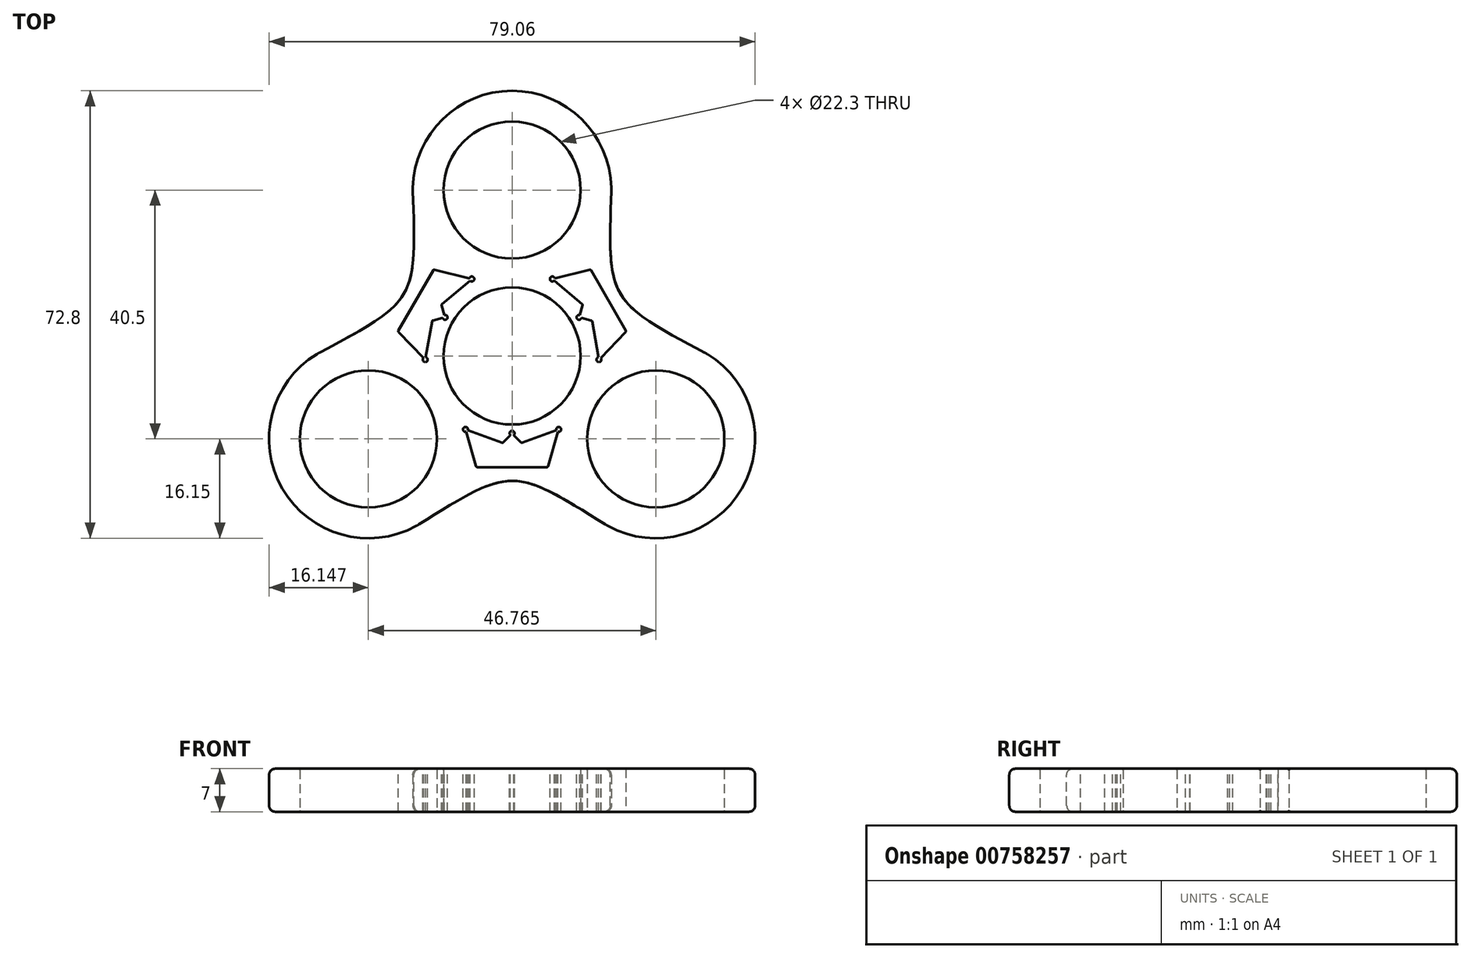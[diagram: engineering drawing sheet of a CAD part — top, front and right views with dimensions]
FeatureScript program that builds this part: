
annotation { "Feature Type Name" : "Feature", "Feature Type Description" : "" }
export const myFeature = defineFeature(function(context is Context, id is Id, definition is map)
    precondition{}
    {
        {
            var Q0;
            Q0=qCreatedBy(makeId("Top.planeOp"),FACE);
            var sketch = newSketch(context, id + "F0", { "sketchPlane" : qUnion([Q0])});
            skCircle(sketch, "E0", {"center": v(0, 0) * mm, "radius": 11.15 * mm});
            skLineSegment(sketch, "E1.0", {"start": v(-15.15, 0) * mm, "end": v(-15.15, 0) * mm});
            skLineSegment(sketch, "E2", {"start": v(0, 0) * mm, "end": v(0, 27) * mm, "construction": true});
            skCircle(sketch, "E3", {"center": v(0, 27) * mm, "radius": 11.15 * mm});
            skArc(sketch, "E4.0", {"start": v(16.15, 27) * mm, "mid": v(0, 43.15) * mm, "end": v(-16.15, 27) * mm});
            skLineSegment(sketch, "E5", {"start": v(-15.15, 0) * mm, "end": v(15.15, 0) * mm, "construction": true});
            skLineSegment(sketch, "E6", {"start": v(-16.15, 27) * mm, "end": v(16.15, 27) * mm, "construction": true});
            skPoint(sketch, "E7.trimOffspring.end.orphan", {"position": v(-15.15, 0) * mm});
            skLineSegment(sketch, "E8", {"start": v(-16.15, 27) * mm, "end": v(-16.15, 27) * mm});
            skArc(sketch, "E9.trimOffspring", {"start": v(-15.15, 0) * mm, "mid": v(0, -15.15) * mm, "end": v(15.15, 0) * mm, "construction": true});
            skLineSegment(sketch, "E10.trimOffspring", {"start": v(16.15, 27) * mm, "end": v(16.15, 27) * mm});
            skLineSegment(sketch, "E11.anchor1", {"start": v(0, 27) * mm, "end": v(0, 43.15) * mm, "construction": true});
            skLineSegment(sketch, "E11.anchor2", {"start": v(0, 27) * mm, "end": v(13.23, 36.26) * mm, "construction": true});
            skLineSegment(sketch, "E12.1.0", {"start": v(7.57, -13.12) * mm, "end": v(-7.58, 13.12) * mm, "construction": true});
            skLineSegment(sketch, "E12.1.2", {"start": v(0, 0) * mm, "end": v(-23.38, -13.5) * mm, "construction": true});
            skLineSegment(sketch, "E12.1.4", {"start": v(-15.3, -27.49) * mm, "end": v(-31.46, 0.49) * mm, "construction": true});
            skCircle(sketch, "E12.1.5", {"center": v(-23.38, -13.5) * mm, "radius": 11.15 * mm});
            skPoint(sketch, "E12.1.9", {"position": v(7.57, -13.12) * mm});
            skArc(sketch, "E12.1.14", {"start": v(-31.46, 0.49) * mm, "mid": v(-37.37, -21.57) * mm, "end": v(-15.3, -27.49) * mm});
            skLineSegment(sketch, "E12.2.0", {"start": v(7.57, 13.12) * mm, "end": v(-7.58, -13.12) * mm, "construction": true});
            skLineSegment(sketch, "E12.2.2", {"start": v(0, 0) * mm, "end": v(23.38, -13.5) * mm, "construction": true});
            skLineSegment(sketch, "E12.2.4", {"start": v(31.46, 0.49) * mm, "end": v(15.3, -27.49) * mm, "construction": true});
            skCircle(sketch, "E12.2.5", {"center": v(23.38, -13.5) * mm, "radius": 11.15 * mm});
            skArc(sketch, "E12.2.12", {"start": v(7.57, 13.12) * mm, "mid": v(-13.12, 7.57) * mm, "end": v(-7.58, -13.12) * mm, "construction": true});
            skArc(sketch, "E12.2.14", {"start": v(15.3, -27.49) * mm, "mid": v(37.37, -21.57) * mm, "end": v(31.46, 0.49) * mm});
            skFitSpline(sketch, "E13", {"points": [v(16.15, 27) * mm, v(31.46, 0.49) * mm], "startDerivative": vector(-1.87, -54.1) * mm, "endDerivative": vector(47.8, -25.43) * mm});
            skLineSegment(sketch, "E14", {"start": v(0, 0) * mm, "end": v(26.97, 15.57) * mm, "construction": true});
            skLineSegment(sketch, "E15", {"start": v(-15.3, -27.49) * mm, "end": v(-3.01, -11.46) * mm});
            skLineSegment(sketch, "E16", {"start": v(-3.01, -11.46) * mm, "end": v(3.36, -11.46) * mm});
            skLineSegment(sketch, "E17", {"start": v(3.36, -11.46) * mm, "end": v(15.3, -27.49) * mm});
            skLineSegment(sketch, "E18", {"start": v(-31.46, 0.49) * mm, "end": v(-13.47, 2.14) * mm});
            skLineSegment(sketch, "E19", {"start": v(-13.47, 2.14) * mm, "end": v(-9.18, 9.2) * mm});
            skLineSegment(sketch, "E20", {"start": v(-9.18, 9.2) * mm, "end": v(-16.15, 27) * mm});
            skSolve(sketch);
        }
        {
            var Q0;
            Q0=qCreatedBy(makeId("Right.planeOp"),FACE);
            var sketch = newSketch(context, id + "F1", { "sketchPlane" : qUnion([Q0])});
            skLineSegment(sketch, "E21", {"start": v(0, 18.91) * mm, "end": v(0, -18.72) * mm, "construction": true});
            skSolve(sketch);
        }
        {
            var Q0;
            Q0=makeQuery(id+"F0.imprint","IMPRINT",FACE,{"disambiguationData":[TD([[makeQuery(id+"F0.imprint","IMPRINT",EDGE,{"derivedFrom":sQuery(id+"F0.wireOp",EDGE,"E0")}),-1.0]])]});
            var Q1;
            Q1=makeQuery(id+"F0.imprint","IMPRINT",FACE,{"disambiguationData":[TD([[makeQuery(id+"F0.imprint","IMPRINT",EDGE,{"derivedFrom":sQuery(id+"F0.wireOp",EDGE,"E3")}),-1.0]])]});
            extrude(context, id + "F2", {"entities" : qUnion([Q0, Q1]), "depth" : 7 * mm, "offsetDistance" : 25 * mm});
        }
        {
            var Q0;
            Q0=makeQuery(id+"F2.opExtrude","SWEPT_BODY",BODY,{"disambiguationData":[OSD([sQuery(id+"F0.wireOp",EDGE,"E0"),sQuery(id+"F0.wireOp",EDGE,"E1.0"),sQuery(id+"F0.wireOp",EDGE,"E3"),sQuery(id+"F0.wireOp",EDGE,"E4.0"),sQuery(id+"F0.wireOp",EDGE,"oIW5whhO-fQ4n-saJ2-gWf4-q0JPziCMkqRt"),sQuery(id+"F0.wireOp",EDGE,"e7664bf7-e720-472f-93c8-efa73fce652a0.MirrorCS"),sQuery(id+"F0.wireOp",EDGE,"15db0cb3-5bd8-46cc-a881-ea2e00802e11.filletArc"),sQuery(id+"F0.wireOp",EDGE,"163ba6b5-26b9-4c58-8659-ca6763b85cf9.filletArc")])]});
            var Q1;
            Q1=sQuery(id+"F1.wireOp",EDGE,"E21");
            circularPattern(context, id + "F3", {"operationType" : NewBodyOperationType.ADD, "entities" : qUnion([Q0]), "axis" : qUnion([Q1]), "angle" : 360 * degree, "instanceCount" : 3, "equalSpace" : true});
        }
        {
            var Q0;
            Q0=makeQuery(id+"F2.opExtrude","SWEPT_EDGE",EDGE,{"disambiguationData":[OSD([sQuery(id+"F0.wireOp",EDGE,"E4.0"),sQuery(id+"F0.wireOp",EDGE,"E13")])]});
            var Q1;
            Q1=makeQuery(id+"F2.opExtrude","SWEPT_EDGE",EDGE,{"disambiguationData":[OSD([sQuery(id+"F0.wireOp",EDGE,"E12.2.14"),sQuery(id+"F0.wireOp",EDGE,"E13")])]});
            var Q2;
            Q2=makeQuery(id+"F3.boolean.opBoolean","MERGE",EDGE,{"derivedFrom":[makeQuery(id+"F2.opExtrude","SWEPT_EDGE",EDGE,{"disambiguationData":[OSD([sQuery(id+"F0.wireOp",EDGE,"E12.2.14"),sQuery(id+"F0.wireOp",EDGE,"E17")])]}),makeQuery(id+"F3.opPattern","COPY",EDGE,{"derivedFrom":makeQuery(id+"F2.opExtrude","SWEPT_EDGE",EDGE,{"disambiguationData":[OSD([sQuery(id+"F0.wireOp",EDGE,"E4.0"),sQuery(id+"F0.wireOp",EDGE,"E13")])]}),"instanceName":"1"})]});
            var Q3;
            Q3=makeQuery(id+"F3.boolean.opBoolean","MERGE",EDGE,{"derivedFrom":[makeQuery(id+"F2.opExtrude","SWEPT_EDGE",EDGE,{"disambiguationData":[OSD([sQuery(id+"F0.wireOp",EDGE,"E12.1.14"),sQuery(id+"F0.wireOp",EDGE,"E15")])]}),makeQuery(id+"F3.opPattern","COPY",EDGE,{"derivedFrom":makeQuery(id+"F2.opExtrude","SWEPT_EDGE",EDGE,{"disambiguationData":[OSD([sQuery(id+"F0.wireOp",EDGE,"E12.2.14"),sQuery(id+"F0.wireOp",EDGE,"E13")])]}),"instanceName":"1"})]});
            var Q4;
            Q4=makeQuery(id+"F3.boolean.opBoolean","MERGE",EDGE,{"derivedFrom":[makeQuery(id+"F2.opExtrude","SWEPT_EDGE",EDGE,{"disambiguationData":[OSD([sQuery(id+"F0.wireOp",EDGE,"E12.1.14"),sQuery(id+"F0.wireOp",EDGE,"E18")])]}),makeQuery(id+"F3.opPattern","COPY",EDGE,{"derivedFrom":makeQuery(id+"F2.opExtrude","SWEPT_EDGE",EDGE,{"disambiguationData":[OSD([sQuery(id+"F0.wireOp",EDGE,"E12.2.14"),sQuery(id+"F0.wireOp",EDGE,"E17")])]}),"instanceName":"1"}),makeQuery(id+"F3.opPattern","COPY",EDGE,{"derivedFrom":makeQuery(id+"F2.opExtrude","SWEPT_EDGE",EDGE,{"disambiguationData":[OSD([sQuery(id+"F0.wireOp",EDGE,"E4.0"),sQuery(id+"F0.wireOp",EDGE,"E13")])]}),"instanceName":"2"})]});
            var Q5;
            Q5=makeQuery(id+"F3.boolean.opBoolean","MERGE",EDGE,{"derivedFrom":[makeQuery(id+"F2.opExtrude","SWEPT_EDGE",EDGE,{"disambiguationData":[OSD([sQuery(id+"F0.wireOp",EDGE,"E4.0"),sQuery(id+"F0.wireOp",EDGE,"E20")])]}),makeQuery(id+"F3.opPattern","COPY",EDGE,{"derivedFrom":makeQuery(id+"F2.opExtrude","SWEPT_EDGE",EDGE,{"disambiguationData":[OSD([sQuery(id+"F0.wireOp",EDGE,"E12.1.14"),sQuery(id+"F0.wireOp",EDGE,"E15")])]}),"instanceName":"1"}),makeQuery(id+"F3.opPattern","COPY",EDGE,{"derivedFrom":makeQuery(id+"F2.opExtrude","SWEPT_EDGE",EDGE,{"disambiguationData":[OSD([sQuery(id+"F0.wireOp",EDGE,"E12.2.14"),sQuery(id+"F0.wireOp",EDGE,"E13")])]}),"instanceName":"2"})]});
            fillet(context, id + "F4", {"entities" : qUnion([Q0, Q1, Q2, Q3, Q4, Q5]), "radius" : 10 * mm, "tangentPropagation" : true, "allowEdgeOverflow" : false});
        }
        {
            var Q0;
            Q0=makeQuery(id+"F2.opExtrude","CAP_EDGE",EDGE,{"disambiguationData":[OSD([sQuery(id+"F0.wireOp",EDGE,"E13")])],"isStart":false});
            var Q1;
            Q1=makeQuery(id+"F3.opPattern","COPY",EDGE,{"derivedFrom":makeQuery(id+"F2.opExtrude","CAP_EDGE",EDGE,{"disambiguationData":[OSD([sQuery(id+"F0.wireOp",EDGE,"E13")])],"isStart":false}),"instanceName":"2"});
            var Q2;
            Q2=makeQuery(id+"F3.opPattern","COPY",EDGE,{"derivedFrom":makeQuery(id+"F2.opExtrude","CAP_EDGE",EDGE,{"disambiguationData":[OSD([sQuery(id+"F0.wireOp",EDGE,"E13")])],"isStart":false}),"instanceName":"1"});
            var Q3;
            Q3=makeQuery(id+"F3.opPattern","COPY",EDGE,{"derivedFrom":makeQuery(id+"F2.opExtrude","CAP_EDGE",EDGE,{"disambiguationData":[OSD([sQuery(id+"F0.wireOp",EDGE,"E13")])],"isStart":true}),"instanceName":"2"});
            var Q4;
            Q4=makeQuery(id+"F2.opExtrude","CAP_EDGE",EDGE,{"disambiguationData":[OSD([sQuery(id+"F0.wireOp",EDGE,"E13")])],"isStart":true});
            fillet(context, id + "F5", {"entities" : qUnion([Q0, Q1, Q2, Q3, Q4]), "radius" : 1 * mm, "tangentPropagation" : true, "allowEdgeOverflow" : false});
        }
        {
            var Q0;
            {var subQ0=makeQuery(id+"F2.opExtrude","CAP_FACE",FACE,{"disambiguationData":[OSD([sQuery(id+"F0.wireOp",EDGE,"E0"),sQuery(id+"F0.wireOp",EDGE,"E3"),sQuery(id+"F0.wireOp",EDGE,"E4.0"),sQuery(id+"F0.wireOp",EDGE,"E12.1.5"),sQuery(id+"F0.wireOp",EDGE,"E12.1.14"),sQuery(id+"F0.wireOp",EDGE,"E12.2.5"),sQuery(id+"F0.wireOp",EDGE,"E12.2.14"),sQuery(id+"F0.wireOp",EDGE,"E13"),sQuery(id+"F0.wireOp",EDGE,"E15"),sQuery(id+"F0.wireOp",EDGE,"E16"),sQuery(id+"F0.wireOp",EDGE,"E17"),sQuery(id+"F0.wireOp",EDGE,"E18"),sQuery(id+"F0.wireOp",EDGE,"E19"),sQuery(id+"F0.wireOp",EDGE,"E20")])],"isStart":false});Q0=makeQuery(id+"F3.boolean.opBoolean","MERGE",FACE,{"derivedFrom":[subQ0,makeQuery(id+"F3.opPattern","COPY",FACE,{"derivedFrom":subQ0,"instanceName":"1"}),makeQuery(id+"F3.opPattern","COPY",FACE,{"derivedFrom":subQ0,"instanceName":"2"})]});}
            var sketch = newSketch(context, id + "F6", { "sketchPlane" : qUnion([Q0])});
            skFitSpline(sketch, "E22.0", {"points": [v(30.8, -0.3) * mm, v(29.52, 0.38) * mm, v(27.61, 1.4) * mm, v(25.08, 2.8) * mm, v(23.2, 3.87) * mm, v(21.38, 5.03) * mm, v(19.92, 6.09) * mm, v(18.81, 7.05) * mm, v(17.78, 8.1) * mm, v(17.02, 9.12) * mm, v(16.5, 10.08) * mm, v(16.17, 10.75) * mm, v(15.84, 11.6) * mm, v(15.54, 12.64) * mm, v(15.25, 14.06) * mm, v(15.05, 15.89) * mm, v(14.96, 18.07) * mm, v(14.96, 20.26) * mm, v(15.02, 23.18) * mm, v(15.1, 25.36) * mm, v(15.14, 26.82) * mm], "construction": true});
            skCircle(sketch, "E23.0", {"center": v(0, 0) * mm, "radius": 11.15 * mm, "construction": true});
            skFitSpline(sketch, "E24.0", {"points": [v(29.62, -2.5) * mm, v(28.99, -2.16) * mm, v(27.7, -1.48) * mm, v(25.79, -0.45) * mm, v(23.86, 0.61) * mm, v(21.92, 1.73) * mm, v(20.31, 2.74) * mm, v(19.02, 3.65) * mm, v(18.06, 4.4) * mm, v(17.1, 5.22) * mm, v(16.18, 6.16) * mm, v(15.33, 7.2) * mm, v(14.59, 8.32) * mm, v(13.95, 9.55) * mm, v(13.47, 10.8) * mm, v(13.11, 12.05) * mm, v(12.77, 13.7) * mm, v(12.55, 15.71) * mm, v(12.46, 18.03) * mm, v(12.46, 20.3) * mm, v(12.52, 23.25) * mm, v(12.6, 25.45) * mm, v(12.64, 26.9) * mm], "construction": true});
            skCircle(sketch, "E25.0", {"center": v(0, 27) * mm, "radius": 11.15 * mm, "construction": true});
            skCircle(sketch, "E26.0", {"center": v(23.38, -13.5) * mm, "radius": 11.15 * mm, "construction": true});
            skArc(sketch, "E27.0", {"start": v(13.54, 1.75) * mm, "mid": v(11.82, 6.83) * mm, "end": v(8.28, 10.85) * mm, "construction": true});
            skArc(sketch, "E28.0", {"start": v(18.57, 4) * mm, "mid": v(15.97, 3.07) * mm, "end": v(13.54, 1.75) * mm, "construction": true});
            skArc(sketch, "E29.0", {"start": v(8.28, 10.85) * mm, "mid": v(10.64, 12.3) * mm, "end": v(12.75, 14.08) * mm, "construction": true});
            skLineSegment(sketch, "E30", {"start": v(12.75, 14.08) * mm, "end": v(18.57, 4) * mm});
            skLineSegment(sketch, "E31", {"start": v(15.66, 9.04) * mm, "end": v(10.9, 6.3) * mm, "construction": true});
            skLineSegment(sketch, "E32", {"start": v(18.57, 4) * mm, "end": v(14.4, -0.3) * mm});
            skLineSegment(sketch, "E33", {"start": v(14.06, -0.2) * mm, "end": v(13, 5.77) * mm});
            skLineSegment(sketch, "E34", {"start": v(13, 5.77) * mm, "end": v(11.28, 6.2) * mm});
            skLineSegment(sketch, "E35.MirrorCS", {"start": v(12.75, 14.08) * mm, "end": v(6.94, 12.63) * mm});
            skLineSegment(sketch, "E36.MirrorCS", {"start": v(11.5, 8.37) * mm, "end": v(11, 6.67) * mm});
            skLineSegment(sketch, "E37.MirrorCS", {"start": v(6.86, 12.28) * mm, "end": v(11.5, 8.37) * mm});
            skLineSegment(sketch, "E38", {"start": v(11.5, 8.37) * mm, "end": v(13, 5.77) * mm, "construction": true});
            skArc(sketch, "E39", {"start": v(14.06, -0.2) * mm, "mid": v(14.02, -0.98) * mm, "end": v(14.4, -0.3) * mm});
            skArc(sketch, "E40", {"start": v(11, 6.67) * mm, "mid": v(10.55, 6.1) * mm, "end": v(11.28, 6.2) * mm});
            skArc(sketch, "E41", {"start": v(6.94, 12.63) * mm, "mid": v(6.16, 12.63) * mm, "end": v(6.86, 12.28) * mm});
            skSolve(sketch);
        }
        {
            var Q0;
            Q0=makeQuery(id+"F6.imprint","IMPRINT",FACE,{"disambiguationData":[TD([[makeQuery(id+"F6.imprint","IMPRINT",EDGE,{"derivedFrom":sQuery(id+"F6.wireOp",EDGE,"E30")}),-1.0]])]});
            var Q1;
            {var subQ0=makeQuery(id+"F2.opExtrude","CAP_FACE",FACE,{"disambiguationData":[OSD([sQuery(id+"F0.wireOp",EDGE,"E0"),sQuery(id+"F0.wireOp",EDGE,"E3"),sQuery(id+"F0.wireOp",EDGE,"E4.0"),sQuery(id+"F0.wireOp",EDGE,"E12.1.5"),sQuery(id+"F0.wireOp",EDGE,"E12.1.14"),sQuery(id+"F0.wireOp",EDGE,"E12.2.5"),sQuery(id+"F0.wireOp",EDGE,"E12.2.14"),sQuery(id+"F0.wireOp",EDGE,"E13"),sQuery(id+"F0.wireOp",EDGE,"E15"),sQuery(id+"F0.wireOp",EDGE,"E16"),sQuery(id+"F0.wireOp",EDGE,"E17"),sQuery(id+"F0.wireOp",EDGE,"E18"),sQuery(id+"F0.wireOp",EDGE,"E19"),sQuery(id+"F0.wireOp",EDGE,"E20")])],"isStart":true});Q1=makeQuery(id+"F3.boolean.opBoolean","MERGE",FACE,{"derivedFrom":[subQ0,makeQuery(id+"F3.opPattern","COPY",FACE,{"derivedFrom":subQ0,"instanceName":"1"}),makeQuery(id+"F3.opPattern","COPY",FACE,{"derivedFrom":subQ0,"instanceName":"2"})]});}
            extrude(context, id + "F7", {"entities" : qUnion([Q0]), "endBound" : BoundingType.UP_TO_SURFACE, "oppositeDirection" : true, "depth" : 25 * mm, "endBoundEntityFace" : qUnion([Q1]), "offsetDistance" : 25 * mm});
        }
        {
            var Q0;
            Q0=qCreatedBy(makeId("Right.planeOp"),FACE);
            var sketch = newSketch(context, id + "F8", { "sketchPlane" : qUnion([Q0])});
            skLineSegment(sketch, "E42", {"start": v(0, 0) * mm, "end": v(0, 16.42) * mm, "construction": true});
            skSolve(sketch);
        }
        {
            var Q0;
            Q0=makeQuery(id+"F7.opExtrude","SWEPT_BODY",BODY,{"disambiguationData":[OSD([sQuery(id+"F6.wireOp",EDGE,"E30"),sQuery(id+"F6.wireOp",EDGE,"E32"),sQuery(id+"F6.wireOp",EDGE,"E33"),sQuery(id+"F6.wireOp",EDGE,"E34"),sQuery(id+"F6.wireOp",EDGE,"E35.MirrorCS"),sQuery(id+"F6.wireOp",EDGE,"E36.MirrorCS"),sQuery(id+"F6.wireOp",EDGE,"E37.MirrorCS"),sQuery(id+"F6.wireOp",EDGE,"E39"),sQuery(id+"F6.wireOp",EDGE,"E40"),sQuery(id+"F6.wireOp",EDGE,"E41")])]});
            var Q1;
            Q1=sQuery(id+"F8.wireOp",EDGE,"E42");
            circularPattern(context, id + "F9", {"operationType" : NewBodyOperationType.REMOVE, "entities" : qUnion([Q0]), "axis" : qUnion([Q1]), "angle" : 360 * degree, "instanceCount" : 3, "equalSpace" : true});
        }
        {
            var Q0;
            Q0=makeQuery(id+"F9.boolean.opBoolean","COPY",EDGE,{"derivedFrom":makeQuery(id+"F7.opExtrude","SWEPT_EDGE",EDGE,{"disambiguationData":[OSD([sQuery(id+"F6.wireOp",EDGE,"E36.MirrorCS"),sQuery(id+"F6.wireOp",EDGE,"E37.MirrorCS")])]})});
            var Q1;
            Q1=makeQuery(id+"F9.boolean.opBoolean","COPY",EDGE,{"derivedFrom":makeQuery(id+"F7.opExtrude","SWEPT_EDGE",EDGE,{"disambiguationData":[OSD([sQuery(id+"F6.wireOp",EDGE,"E33"),sQuery(id+"F6.wireOp",EDGE,"E34")])]})});
            var Q2;
            Q2=makeQuery(id+"F9.boolean.opBoolean","COPY",EDGE,{"derivedFrom":makeQuery(id+"F7.opExtrude","SWEPT_EDGE",EDGE,{"disambiguationData":[OSD([sQuery(id+"F6.wireOp",EDGE,"E30"),sQuery(id+"F6.wireOp",EDGE,"E35.MirrorCS")])]})});
            var Q3;
            Q3=makeQuery(id+"F9.boolean.opBoolean","COPY",EDGE,{"derivedFrom":makeQuery(id+"F7.opExtrude","SWEPT_EDGE",EDGE,{"disambiguationData":[OSD([sQuery(id+"F6.wireOp",EDGE,"E30"),sQuery(id+"F6.wireOp",EDGE,"E32")])]})});
            var Q4;
            Q4=makeQuery(id+"F9.boolean.opBoolean","COPY",EDGE,{"derivedFrom":makeQuery(id+"F9.opPattern","COPY",EDGE,{"derivedFrom":makeQuery(id+"F7.opExtrude","SWEPT_EDGE",EDGE,{"disambiguationData":[OSD([sQuery(id+"F6.wireOp",EDGE,"E36.MirrorCS"),sQuery(id+"F6.wireOp",EDGE,"E37.MirrorCS")])]}),"instanceName":"2"})});
            var Q5;
            Q5=makeQuery(id+"F9.boolean.opBoolean","COPY",EDGE,{"derivedFrom":makeQuery(id+"F9.opPattern","COPY",EDGE,{"derivedFrom":makeQuery(id+"F7.opExtrude","SWEPT_EDGE",EDGE,{"disambiguationData":[OSD([sQuery(id+"F6.wireOp",EDGE,"E33"),sQuery(id+"F6.wireOp",EDGE,"E34")])]}),"instanceName":"2"})});
            var Q6;
            Q6=makeQuery(id+"F9.boolean.opBoolean","COPY",EDGE,{"derivedFrom":makeQuery(id+"F9.opPattern","COPY",EDGE,{"derivedFrom":makeQuery(id+"F7.opExtrude","SWEPT_EDGE",EDGE,{"disambiguationData":[OSD([sQuery(id+"F6.wireOp",EDGE,"E30"),sQuery(id+"F6.wireOp",EDGE,"E35.MirrorCS")])]}),"instanceName":"2"})});
            var Q7;
            Q7=makeQuery(id+"F9.boolean.opBoolean","COPY",EDGE,{"derivedFrom":makeQuery(id+"F9.opPattern","COPY",EDGE,{"derivedFrom":makeQuery(id+"F7.opExtrude","SWEPT_EDGE",EDGE,{"disambiguationData":[OSD([sQuery(id+"F6.wireOp",EDGE,"E30"),sQuery(id+"F6.wireOp",EDGE,"E32")])]}),"instanceName":"2"})});
            var Q8;
            Q8=makeQuery(id+"F9.boolean.opBoolean","COPY",EDGE,{"derivedFrom":makeQuery(id+"F9.opPattern","COPY",EDGE,{"derivedFrom":makeQuery(id+"F7.opExtrude","SWEPT_EDGE",EDGE,{"disambiguationData":[OSD([sQuery(id+"F6.wireOp",EDGE,"E36.MirrorCS"),sQuery(id+"F6.wireOp",EDGE,"E37.MirrorCS")])]}),"instanceName":"1"})});
            var Q9;
            Q9=makeQuery(id+"F9.boolean.opBoolean","COPY",EDGE,{"derivedFrom":makeQuery(id+"F9.opPattern","COPY",EDGE,{"derivedFrom":makeQuery(id+"F7.opExtrude","SWEPT_EDGE",EDGE,{"disambiguationData":[OSD([sQuery(id+"F6.wireOp",EDGE,"E33"),sQuery(id+"F6.wireOp",EDGE,"E34")])]}),"instanceName":"1"})});
            var Q10;
            Q10=makeQuery(id+"F9.boolean.opBoolean","COPY",EDGE,{"derivedFrom":makeQuery(id+"F9.opPattern","COPY",EDGE,{"derivedFrom":makeQuery(id+"F7.opExtrude","SWEPT_EDGE",EDGE,{"disambiguationData":[OSD([sQuery(id+"F6.wireOp",EDGE,"E30"),sQuery(id+"F6.wireOp",EDGE,"E32")])]}),"instanceName":"1"})});
            var Q11;
            Q11=makeQuery(id+"F9.boolean.opBoolean","COPY",EDGE,{"derivedFrom":makeQuery(id+"F9.opPattern","COPY",EDGE,{"derivedFrom":makeQuery(id+"F7.opExtrude","SWEPT_EDGE",EDGE,{"disambiguationData":[OSD([sQuery(id+"F6.wireOp",EDGE,"E30"),sQuery(id+"F6.wireOp",EDGE,"E35.MirrorCS")])]}),"instanceName":"1"})});
            fillet(context, id + "F10", {"entities" : qUnion([Q0, Q1, Q2, Q3, Q4, Q5, Q6, Q7, Q8, Q9, Q10, Q11]), "radius" : 0.2 * mm, "tangentPropagation" : true, "allowEdgeOverflow" : false});
        }
        {
            var Q0;
            Q0=makeQuery(id+"F2.opExtrude","SWEPT_FACE",FACE,{"disambiguationData":[OSD([sQuery(id+"F0.wireOp",EDGE,"E0")])]});
            var Q1;
            Q1=makeQuery(id+"F2.opExtrude","SWEPT_FACE",FACE,{"disambiguationData":[OSD([sQuery(id+"F0.wireOp",EDGE,"E12.2.5")])]});
            var Q2;
            Q2=makeQuery(id+"F2.opExtrude","SWEPT_FACE",FACE,{"disambiguationData":[OSD([sQuery(id+"F0.wireOp",EDGE,"E12.1.5")])]});
            var Q3;
            Q3=makeQuery(id+"F2.opExtrude","SWEPT_FACE",FACE,{"disambiguationData":[OSD([sQuery(id+"F0.wireOp",EDGE,"E3")])]});
            var Q4;
            Q4=makeQuery(id+"F9.boolean.opBoolean","COPY",EDGE,{"derivedFrom":makeQuery(id+"F9.opPattern","COPY",EDGE,{"derivedFrom":makeQuery(id+"F7.opExtrude","CAP_EDGE",EDGE,{"disambiguationData":[OSD([sQuery(id+"F6.wireOp",EDGE,"E27.0")])],"isStart":true}),"instanceName":"1"})});
            var Q5;
            Q5=makeQuery(id+"F9.boolean.opBoolean","COPY",EDGE,{"derivedFrom":makeQuery(id+"F7.opExtrude","CAP_EDGE",EDGE,{"disambiguationData":[OSD([sQuery(id+"F6.wireOp",EDGE,"E27.0")])],"isStart":true})});
            var Q6;
            Q6=makeQuery(id+"F9.boolean.opBoolean","COPY",EDGE,{"derivedFrom":makeQuery(id+"F9.opPattern","COPY",EDGE,{"derivedFrom":makeQuery(id+"F7.opExtrude","CAP_EDGE",EDGE,{"disambiguationData":[OSD([sQuery(id+"F6.wireOp",EDGE,"E24.0")])],"isStart":true}),"instanceName":"2"})});
            var Q7;
            {var subQ0=makeQuery(id+"F2.opExtrude","CAP_FACE",FACE,{"disambiguationData":[OSD([sQuery(id+"F0.wireOp",EDGE,"E0"),sQuery(id+"F0.wireOp",EDGE,"E3"),sQuery(id+"F0.wireOp",EDGE,"E4.0"),sQuery(id+"F0.wireOp",EDGE,"E12.1.5"),sQuery(id+"F0.wireOp",EDGE,"E12.1.14"),sQuery(id+"F0.wireOp",EDGE,"E12.2.5"),sQuery(id+"F0.wireOp",EDGE,"E12.2.14"),sQuery(id+"F0.wireOp",EDGE,"E13"),sQuery(id+"F0.wireOp",EDGE,"E15"),sQuery(id+"F0.wireOp",EDGE,"E16"),sQuery(id+"F0.wireOp",EDGE,"E17"),sQuery(id+"F0.wireOp",EDGE,"E18"),sQuery(id+"F0.wireOp",EDGE,"E19"),sQuery(id+"F0.wireOp",EDGE,"E20")])],"isStart":true});Q7=makeQuery(id+"F9.boolean.opBoolean","COPY",EDGE,{"derivedFrom":makeQuery(id+"F9.opPattern","COPY",EDGE,{"derivedFrom":makeQuery(id+"F7.opExtrude","TWEAK_EDGE",EDGE,{"derivedFrom":[makeQuery(id+"F3.boolean.opBoolean","MERGE",FACE,{"derivedFrom":[subQ0,makeQuery(id+"F3.opPattern","COPY",FACE,{"derivedFrom":subQ0,"instanceName":"1"}),makeQuery(id+"F3.opPattern","COPY",FACE,{"derivedFrom":subQ0,"instanceName":"2"})]}),makeQuery(id+"F6.imprint","IMPRINT",EDGE,{"derivedFrom":sQuery(id+"F6.wireOp",EDGE,"E24.0")})]}),"instanceName":"2"})});}
            var Q8;
            {var subQ0=makeQuery(id+"F2.opExtrude","CAP_FACE",FACE,{"disambiguationData":[OSD([sQuery(id+"F0.wireOp",EDGE,"E0"),sQuery(id+"F0.wireOp",EDGE,"E3"),sQuery(id+"F0.wireOp",EDGE,"E4.0"),sQuery(id+"F0.wireOp",EDGE,"E12.1.5"),sQuery(id+"F0.wireOp",EDGE,"E12.1.14"),sQuery(id+"F0.wireOp",EDGE,"E12.2.5"),sQuery(id+"F0.wireOp",EDGE,"E12.2.14"),sQuery(id+"F0.wireOp",EDGE,"E13"),sQuery(id+"F0.wireOp",EDGE,"E15"),sQuery(id+"F0.wireOp",EDGE,"E16"),sQuery(id+"F0.wireOp",EDGE,"E17"),sQuery(id+"F0.wireOp",EDGE,"E18"),sQuery(id+"F0.wireOp",EDGE,"E19"),sQuery(id+"F0.wireOp",EDGE,"E20")])],"isStart":true});Q8=makeQuery(id+"F9.boolean.opBoolean","COPY",EDGE,{"derivedFrom":makeQuery(id+"F9.opPattern","COPY",EDGE,{"derivedFrom":makeQuery(id+"F7.opExtrude","TWEAK_EDGE",EDGE,{"derivedFrom":[makeQuery(id+"F3.boolean.opBoolean","MERGE",FACE,{"derivedFrom":[subQ0,makeQuery(id+"F3.opPattern","COPY",FACE,{"derivedFrom":subQ0,"instanceName":"1"}),makeQuery(id+"F3.opPattern","COPY",FACE,{"derivedFrom":subQ0,"instanceName":"2"})]}),makeQuery(id+"F6.imprint","IMPRINT",EDGE,{"derivedFrom":sQuery(id+"F6.wireOp",EDGE,"E27.0")})]}),"instanceName":"1"})});}
            var Q9;
            {var subQ0=makeQuery(id+"F2.opExtrude","CAP_FACE",FACE,{"disambiguationData":[OSD([sQuery(id+"F0.wireOp",EDGE,"E0"),sQuery(id+"F0.wireOp",EDGE,"E3"),sQuery(id+"F0.wireOp",EDGE,"E4.0"),sQuery(id+"F0.wireOp",EDGE,"E12.1.5"),sQuery(id+"F0.wireOp",EDGE,"E12.1.14"),sQuery(id+"F0.wireOp",EDGE,"E12.2.5"),sQuery(id+"F0.wireOp",EDGE,"E12.2.14"),sQuery(id+"F0.wireOp",EDGE,"E13"),sQuery(id+"F0.wireOp",EDGE,"E15"),sQuery(id+"F0.wireOp",EDGE,"E16"),sQuery(id+"F0.wireOp",EDGE,"E17"),sQuery(id+"F0.wireOp",EDGE,"E18"),sQuery(id+"F0.wireOp",EDGE,"E19"),sQuery(id+"F0.wireOp",EDGE,"E20")])],"isStart":true});Q9=makeQuery(id+"F9.boolean.opBoolean","COPY",EDGE,{"derivedFrom":makeQuery(id+"F7.opExtrude","TWEAK_EDGE",EDGE,{"derivedFrom":[makeQuery(id+"F3.boolean.opBoolean","MERGE",FACE,{"derivedFrom":[subQ0,makeQuery(id+"F3.opPattern","COPY",FACE,{"derivedFrom":subQ0,"instanceName":"1"}),makeQuery(id+"F3.opPattern","COPY",FACE,{"derivedFrom":subQ0,"instanceName":"2"})]}),makeQuery(id+"F6.imprint","IMPRINT",EDGE,{"derivedFrom":sQuery(id+"F6.wireOp",EDGE,"E27.0")})]})});}
            fillet(context, id + "F11", {"entities" : qUnion([Q0, Q1, Q2, Q3, Q4, Q5, Q6, Q7, Q8, Q9]), "radius" : 0.2 * mm, "tangentPropagation" : true, "allowEdgeOverflow" : false});
        }
    });
